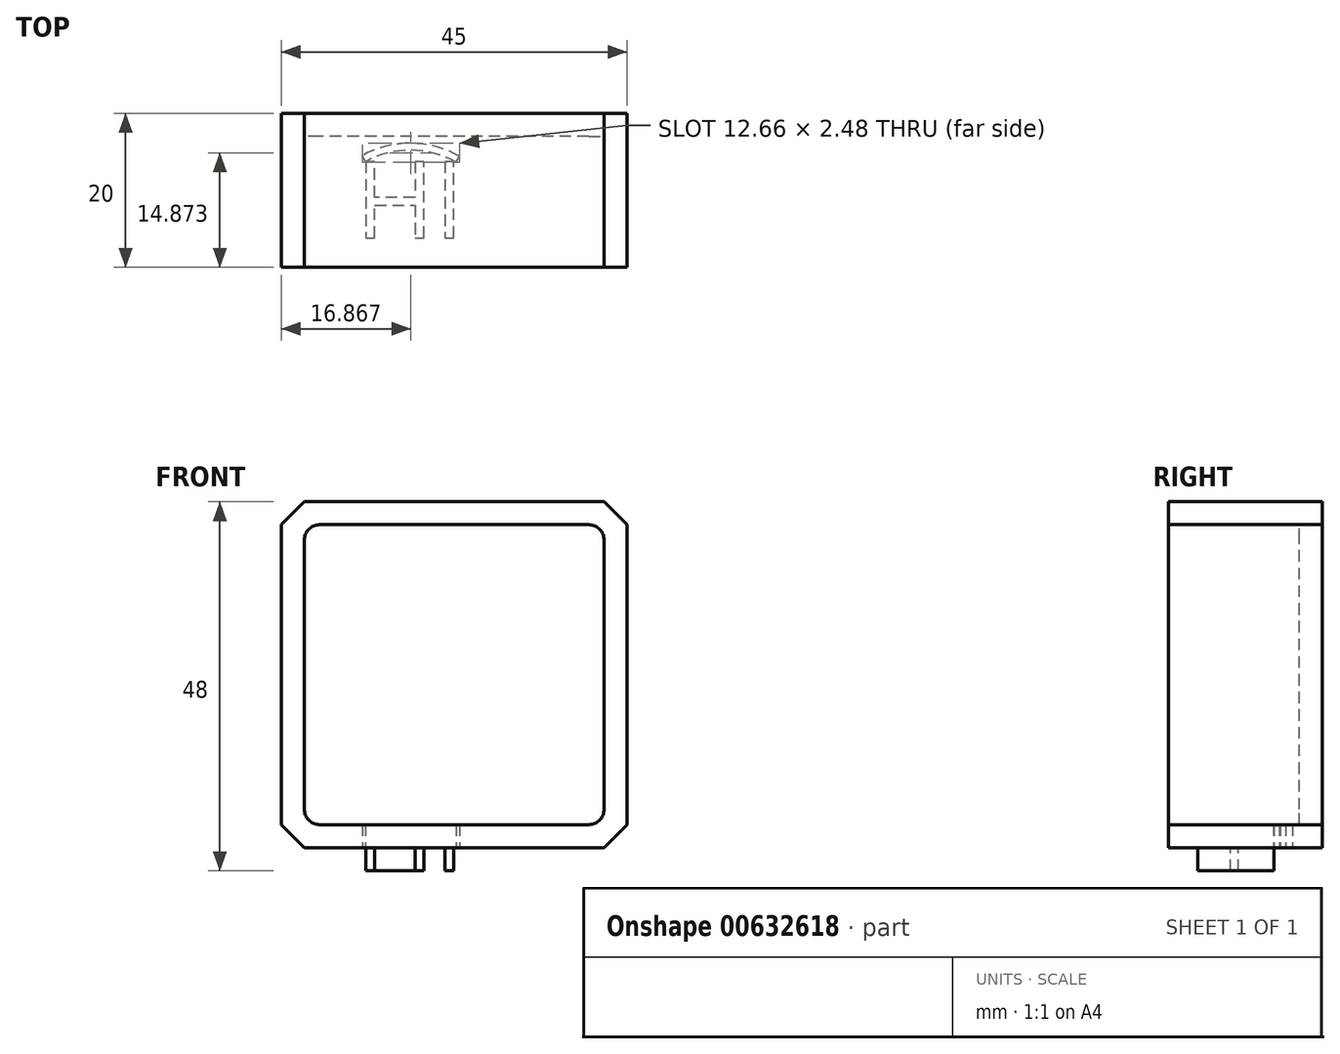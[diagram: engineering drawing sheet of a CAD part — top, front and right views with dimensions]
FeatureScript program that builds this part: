
annotation { "Feature Type Name" : "Feature", "Feature Type Description" : "" }
export const myFeature = defineFeature(function(context is Context, id is Id, definition is map)
    precondition{}
    {
        {
            var Q0;
            Q0=qCreatedBy(makeId("Front.planeOp"),FACE);
            var sketch = newSketch(context, id + "F0", { "sketchPlane" : qUnion([Q0])});
            skLineSegment(sketch, "E0.bottom", {"start": v(-22.5, 22.5) * mm, "end": v(22.5, 22.5) * mm});
            skLineSegment(sketch, "E0.top", {"start": v(-22.5, -22.5) * mm, "end": v(22.5, -22.5) * mm});
            skLineSegment(sketch, "E0.left", {"start": v(-22.5, 22.5) * mm, "end": v(-22.5, -22.5) * mm});
            skLineSegment(sketch, "E0.right", {"start": v(22.5, 22.5) * mm, "end": v(22.5, -22.5) * mm});
            skPoint(sketch, "E0.middle", {"position": v(0, 0) * mm});
            skSolve(sketch);
        }
        {
            var Q0;
            Q0=makeQuery(id+"F0.imprint","IMPRINT",FACE,{"disambiguationData":[TD([[makeQuery(id+"F0.imprint","IMPRINT",EDGE,{"derivedFrom":sQuery(id+"F0.wireOp",EDGE,"E0.bottom")}),-1.0]])]});
            extrude(context, id + "F1", {"entities" : qUnion([Q0]), "depth" : 20 * mm, "offsetDistance" : 25 * mm});
        }
        {
            var Q0;
            Q0=makeQuery(id+"F1.opExtrude","CAP_FACE",FACE,{"disambiguationData":[OSD([sQuery(id+"F0.wireOp",EDGE,"E0.bottom"),sQuery(id+"F0.wireOp",EDGE,"E0.top"),sQuery(id+"F0.wireOp",EDGE,"E0.left"),sQuery(id+"F0.wireOp",EDGE,"E0.right")])],"isStart":false});
            var sketch = newSketch(context, id + "F2", { "sketchPlane" : qUnion([Q0])});
            skLineSegment(sketch, "E1.0", {"start": v(-19.5, 19.5) * mm, "end": v(19.5, 19.5) * mm});
            skLineSegment(sketch, "E1.1", {"start": v(-19.5, 19.5) * mm, "end": v(-19.5, -19.5) * mm});
            skLineSegment(sketch, "E1.2", {"start": v(-19.5, -19.5) * mm, "end": v(19.5, -19.5) * mm});
            skLineSegment(sketch, "E1.3", {"start": v(19.5, 19.5) * mm, "end": v(19.5, -19.5) * mm});
            skSolve(sketch);
        }
        {
            var Q0;
            Q0=makeQuery(id+"F2.imprint","IMPRINT",FACE,{"disambiguationData":[TD([[makeQuery(id+"F2.imprint","IMPRINT",EDGE,{"derivedFrom":sQuery(id+"F2.wireOp",EDGE,"E1.0")}),-1.0]])]});
            var Q1;
            Q1=makeQuery(id+"F1.opExtrude","CAP_FACE",FACE,{"disambiguationData":[OSD([sQuery(id+"F0.wireOp",EDGE,"E0.bottom"),sQuery(id+"F0.wireOp",EDGE,"E0.top"),sQuery(id+"F0.wireOp",EDGE,"E0.left"),sQuery(id+"F0.wireOp",EDGE,"E0.right")])],"isStart":true});
            extrude(context, id + "F3", {"entities" : qUnion([Q0]), "operationType" : NewBodyOperationType.REMOVE, "endBound" : BoundingType.UP_TO_SURFACE, "oppositeDirection" : true, "depth" : 25 * mm, "endBoundEntityFace" : qUnion([Q1]), "hasOffset" : true, "offsetDistance" : 3 * mm});
        }
        {
            var Q0;
            Q0=makeQuery(id+"F3.boolean.opBoolean","COPY",EDGE,{"derivedFrom":makeQuery(id+"F3.opExtrude","SWEPT_EDGE",EDGE,{"disambiguationData":[OSD([sQuery(id+"F2.wireOp",EDGE,"E1.0"),sQuery(id+"F2.wireOp",EDGE,"E1.3")])]})});
            var Q1;
            Q1=makeQuery(id+"F3.boolean.opBoolean","COPY",EDGE,{"derivedFrom":makeQuery(id+"F3.opExtrude","SWEPT_EDGE",EDGE,{"disambiguationData":[OSD([sQuery(id+"F2.wireOp",EDGE,"E1.0"),sQuery(id+"F2.wireOp",EDGE,"E1.1")])]})});
            var Q2;
            Q2=makeQuery(id+"F3.boolean.opBoolean","COPY",EDGE,{"derivedFrom":makeQuery(id+"F3.opExtrude","SWEPT_EDGE",EDGE,{"disambiguationData":[OSD([sQuery(id+"F2.wireOp",EDGE,"E1.1"),sQuery(id+"F2.wireOp",EDGE,"E1.2")])]})});
            var Q3;
            Q3=makeQuery(id+"F3.boolean.opBoolean","COPY",EDGE,{"derivedFrom":makeQuery(id+"F3.opExtrude","SWEPT_EDGE",EDGE,{"disambiguationData":[OSD([sQuery(id+"F2.wireOp",EDGE,"E1.2"),sQuery(id+"F2.wireOp",EDGE,"E1.3")])]})});
            fillet(context, id + "F4", {"entities" : qUnion([Q0, Q1, Q2, Q3]), "radius" : 2 * mm, "tangentPropagation" : true, "allowEdgeOverflow" : false});
        }
        {
            var Q0;
            Q0=makeQuery(id+"F1.opExtrude","SWEPT_EDGE",EDGE,{"disambiguationData":[OSD([sQuery(id+"F0.wireOp",EDGE,"E0.bottom"),sQuery(id+"F0.wireOp",EDGE,"E0.right")])]});
            var Q1;
            Q1=makeQuery(id+"F1.opExtrude","SWEPT_EDGE",EDGE,{"disambiguationData":[OSD([sQuery(id+"F0.wireOp",EDGE,"E0.bottom"),sQuery(id+"F0.wireOp",EDGE,"E0.left")])]});
            var Q2;
            Q2=makeQuery(id+"F1.opExtrude","SWEPT_EDGE",EDGE,{"disambiguationData":[OSD([sQuery(id+"F0.wireOp",EDGE,"E0.top"),sQuery(id+"F0.wireOp",EDGE,"E0.left")])]});
            var Q3;
            Q3=makeQuery(id+"F1.opExtrude","SWEPT_EDGE",EDGE,{"disambiguationData":[OSD([sQuery(id+"F0.wireOp",EDGE,"E0.top"),sQuery(id+"F0.wireOp",EDGE,"E0.right")])]});
            chamfer(context, id + "F5", {"entities" : qUnion([Q0, Q1, Q2, Q3]), "width" : 3 * mm, "tangentPropagation" : true});
        }
        {
            var Q0;
            Q0=makeQuery(id+"F1.opExtrude","SWEPT_FACE",FACE,{"disambiguationData":[OSD([sQuery(id+"F0.wireOp",EDGE,"E0.top")])]});
            var sketch = newSketch(context, id + "F6", { "sketchPlane" : qUnion([Q0])});
            skText(sketch, "E2", { "text": "HI", "fontName": "OpenSans-Regular.ttf"});
            skArc(sketch, "E3", {"start": v(-11.53, 6.26) * mm, "mid": v(-5.63, 4.79) * mm, "end": v(0.25, 6.37) * mm});
            skArc(sketch, "E4.0", {"start": v(-11.96, 5.47) * mm, "mid": v(-5.62, 3.89) * mm, "end": v(0.7, 5.58) * mm});
            skLineSegment(sketch, "E5", {"start": v(-11.53, 6.26) * mm, "end": v(-11.96, 5.47) * mm});
            skLineSegment(sketch, "E6", {"start": v(0.25, 6.37) * mm, "end": v(0.7, 5.58) * mm});
            const initialGuessF6  = {"E2": [-0.01284, 0.00626, 1, 0, 0.01]};
            skSetInitialGuess(sketch, initialGuessF6);
            skSolve(sketch);
        }
        {
            var Q0;
            Q0=makeQuery(id+"F6.imprint","IMPRINT",FACE,{"disambiguationData":[TD([[makeQuery(id+"F6.imprint","IMPRINT",EDGE,{"derivedFrom":sQuery(id+"F6.wireOp",EDGE,"E2.sketch_text.stroke-0")}),-1.0]])]});
            var Q1;
            Q1=makeQuery(id+"F6.imprint","IMPRINT",FACE,{"disambiguationData":[TD([[makeQuery(id+"F6.imprint","IMPRINT",EDGE,{"derivedFrom":sQuery(id+"F6.wireOp",EDGE,"E2.sketch_text.stroke-12")}),-1.0]])]});
            extrude(context, id + "F7", {"entities" : qUnion([Q0, Q1]), "operationType" : NewBodyOperationType.ADD, "depth" : 3 * mm, "offsetDistance" : 25 * mm});
        }
        {
            var Q0;
            Q0=makeQuery(id+"F6.imprint","IMPRINT",FACE,{"disambiguationData":[TD([[makeQuery(id+"F6.imprint","IMPRINT",EDGE,{"derivedFrom":sQuery(id+"F6.wireOp",EDGE,"E3")}),-1.0]])]});
            var Q1;
            Q1=makeQuery(id+"F3.boolean.opBoolean","COPY",FACE,{"derivedFrom":makeQuery(id+"F3.opExtrude","SWEPT_FACE",FACE,{"disambiguationData":[OSD([sQuery(id+"F2.wireOp",EDGE,"E1.2")])]})});
            extrude(context, id + "F8", {"entities" : qUnion([Q0]), "operationType" : NewBodyOperationType.REMOVE, "endBound" : BoundingType.UP_TO_SURFACE, "oppositeDirection" : true, "depth" : 25 * mm, "endBoundEntityFace" : qUnion([Q1]), "offsetDistance" : 25 * mm});
        }
    });
